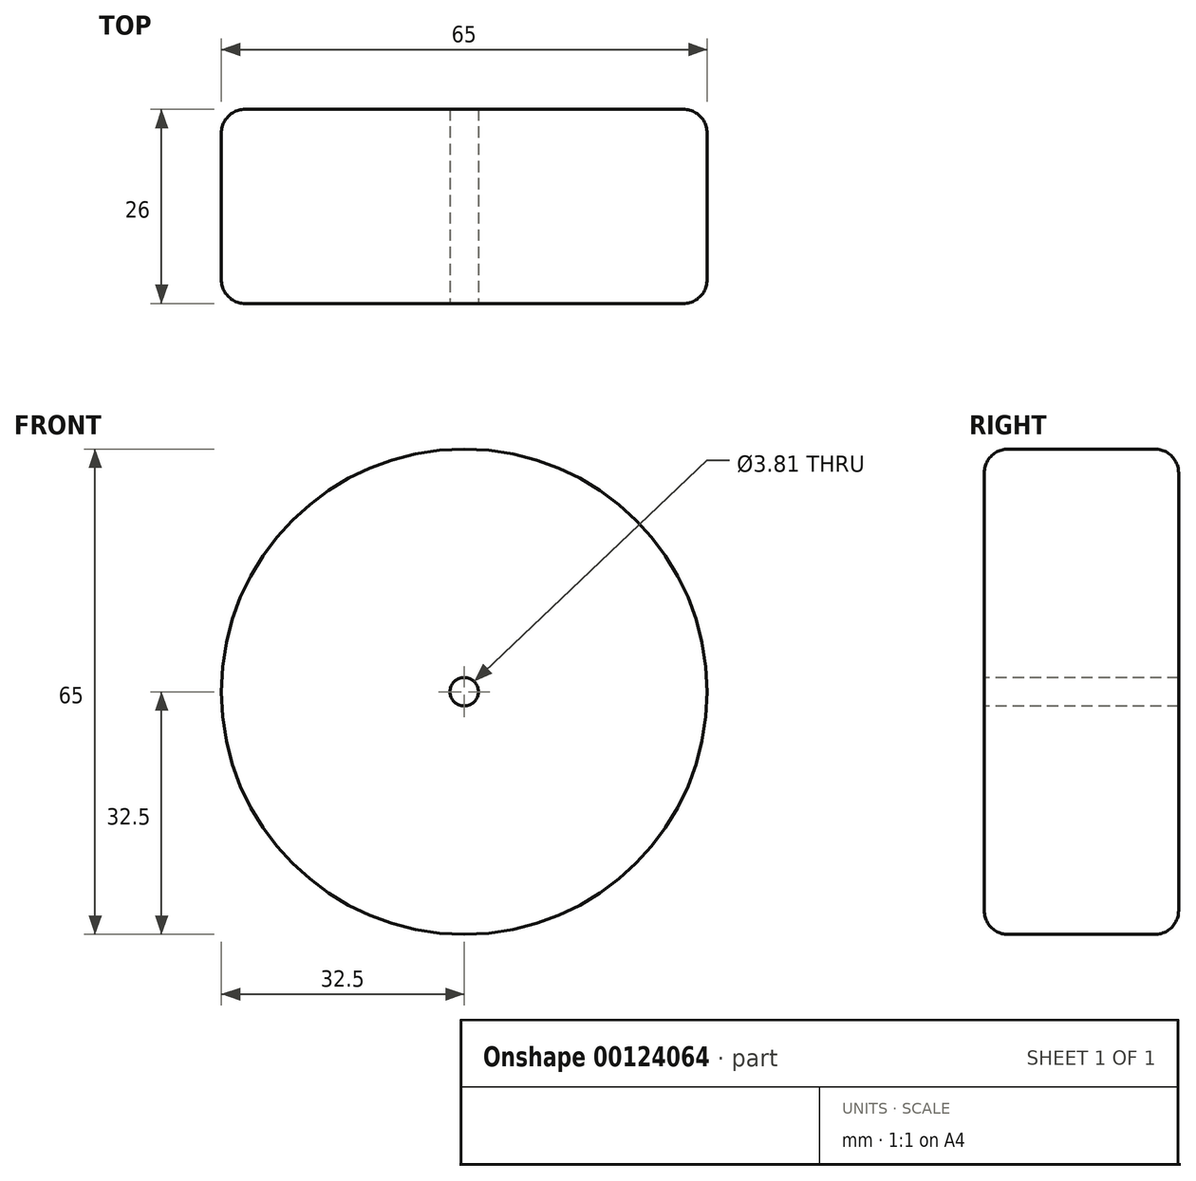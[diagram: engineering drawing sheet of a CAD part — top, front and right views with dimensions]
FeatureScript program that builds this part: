
annotation { "Feature Type Name" : "Feature", "Feature Type Description" : "" }
export const myFeature = defineFeature(function(context is Context, id is Id, definition is map)
    precondition{}
    {
        {
            var Q0;
            Q0=qCreatedBy(makeId("Front.planeOp"),FACE);
            var sketch = newSketch(context, id + "F0", { "sketchPlane" : qUnion([Q0])});
            skCircle(sketch, "E0", {"center": v(0, 0) * mm, "radius": 32.5 * mm});
            skSolve(sketch);
        }
        {
            var Q0;
            Q0=makeQuery(id+"F0.imprint","IMPRINT",FACE,{"disambiguationData":[TD([[makeQuery(id+"F0.imprint","IMPRINT",EDGE,{"derivedFrom":sQuery(id+"F0.wireOp",EDGE,"E0")}),1.0]])]});
            extrude(context, id + "F1", {"entities" : qUnion([Q0]), "depth" : 26 * mm});
        }
        {
            var Q0;
            Q0=makeQuery(id+"F1.opExtrude","CAP_EDGE",EDGE,{"disambiguationData":[OSD([sQuery(id+"F0.wireOp",EDGE,"E0")])],"isStart":false});
            var Q1;
            Q1=makeQuery(id+"F1.opExtrude","CAP_EDGE",EDGE,{"disambiguationData":[OSD([sQuery(id+"F0.wireOp",EDGE,"E0")])],"isStart":true});
            fillet(context, id + "F2", {"entities" : qUnion([Q0, Q1]), "radius" : 3.17 * mm, "tangentPropagation" : true, "allowEdgeOverflow" : false});
        }
        {
            var Q0;
            Q0=makeQuery(id+"F1.opExtrude","CAP_FACE",FACE,{"disambiguationData":[OSD([sQuery(id+"F0.wireOp",EDGE,"E0")])],"isStart":false});
            var sketch = newSketch(context, id + "F3", { "sketchPlane" : qUnion([Q0])});
            skPoint(sketch, "E1", {"position": v(0, 0) * mm});
            skSolve(sketch);
        }
        {
            var Q0;
            Q0=sQuery(id+"F3.wireOp",VERTEX,"E1");
            var Q1;
            Q1=makeQuery(id+"F1.opExtrude","SWEPT_BODY",BODY,{"disambiguationData":[OSD([sQuery(id+"F0.wireOp",EDGE,"E0")])]});
            hole(context, id + "F4", {"style" : HoleStyle.SIMPLE, "endStyle" : HoleEndStyle.THROUGH, "holeDiameter" : 3.8 * mm, "locations" : qUnion([Q0]), "scope" : qUnion([Q1]), "isTappedThrough" : true});
        }
    });
